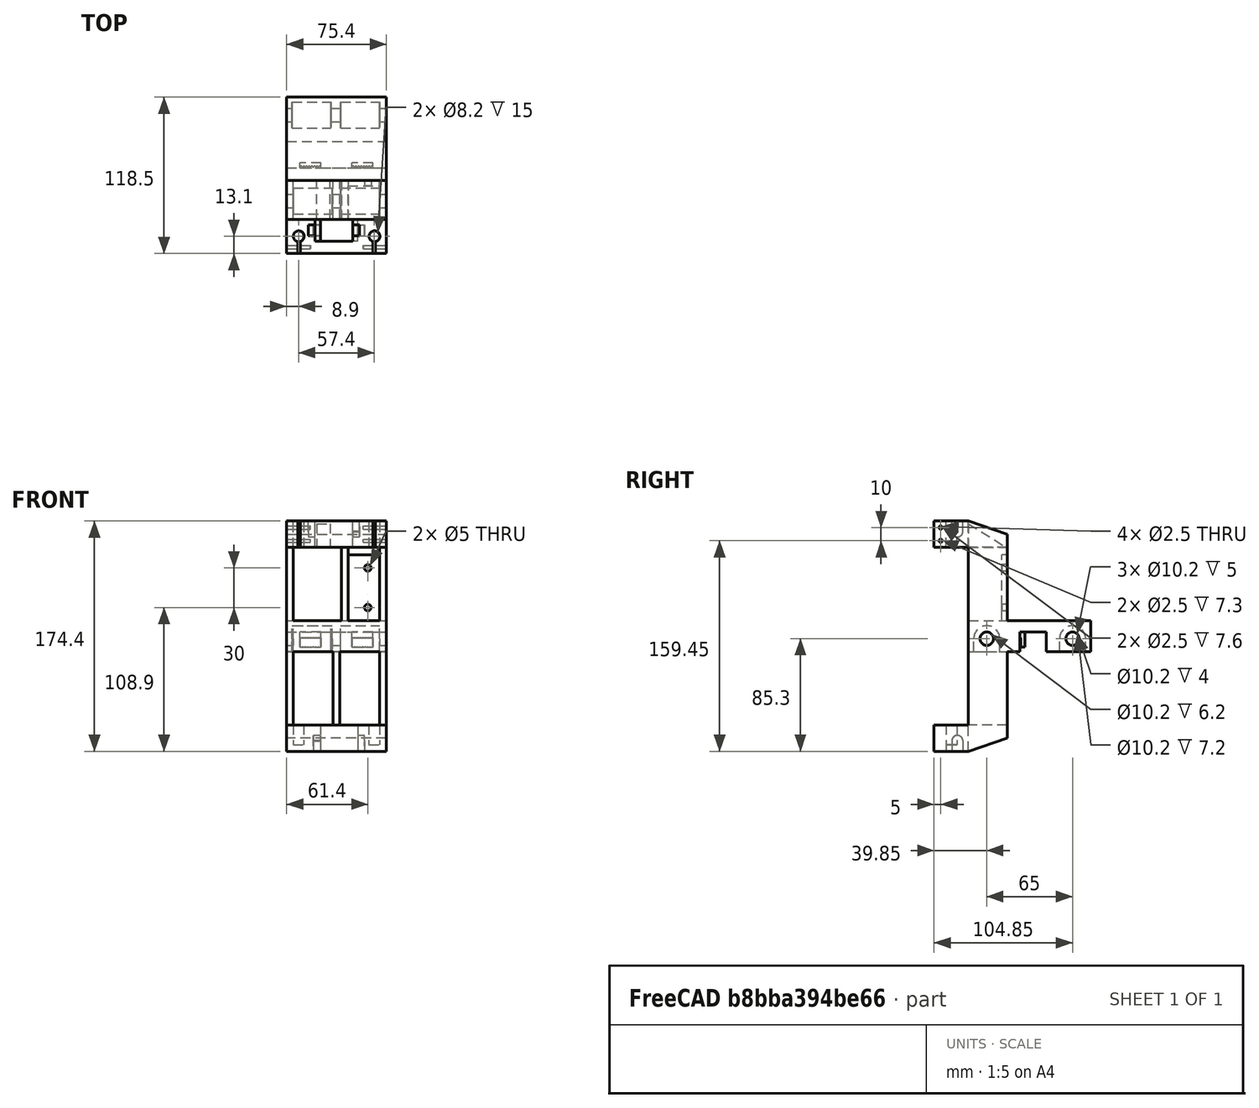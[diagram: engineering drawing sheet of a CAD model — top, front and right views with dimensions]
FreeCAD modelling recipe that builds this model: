
FCSTD DOCUMENT  (FreeCAD 0.18R16110 (Git))
Label: z-support
License: All rights reserved
LicenseURL: http://en.wikipedia.org/wiki/All_rights_reserved
objects: Part::Cut×25, Part::Cylinder×15, Part::Box×13, Part::MultiFuse×11, Part::Wedge×8, Part::Extrusion×8, Spreadsheet::Sheet×2, Sketcher::SketchObject×1, Mesh::Feature×1
note: 81 computed .brp shape members not serialized (recipe doc carries the construction recipe); baked Part::Feature solids carry a one-line shape summary decoded from their .brp

FEATURE [Part::Box] Box007  label="Quader004"
  AttacherType = Attacher::AttachEngine3D
  Height = 10
  Length = 5.2
  Placement = pos=(0,-4.1,0) rot=(0,0,1;0rad)
  Width = 8.2
  expr: Placement.Base.y = -Spreadsheet.z_dbohrung / 2 - Spreadsheet.tolerance / 2
  expr: Height = Spreadsheet.z_hmount / 2
  expr: Width = Spreadsheet.z_dbohrung + Spreadsheet.tolerance
  expr: Length = Spreadsheet.z_lbohrung + Spreadsheet.tolerance
FEATURE [Part::Box] Box012  label="Quader009"
  AttacherType = Attacher::AttachEngine3D
  Height = 9.85
  Length = 29.6
  Placement = pos=(0,-9.85,-9.85) rot=(0,0,1;0rad)
  Width = 19.7
  expr: Placement.Base.z = -Spreadsheet.x_dlinear / 2 - Spreadsheet.tolerance / 2
  expr: Height = Spreadsheet.x_dlinear / 2 + Spreadsheet.tolerance / 2
  expr: Placement.Base.y = -Spreadsheet.x_dlinear / 2 - Spreadsheet.tolerance / 2
  expr: Width = Spreadsheet.x_dlinear + Spreadsheet.tolerance
  expr: Length = Spreadsheet.x_hlinear + Spreadsheet.tolerance
FEATURE [Part::Box] Box008  label="Quader005"
  AttacherType = Attacher::AttachEngine3D
  Height = 10
  Length = 5.2
  Placement = pos=(0,-4.05,0) rot=(0,0,1;0rad)
  Width = 8.2
  expr: Width = Spreadsheet.z_dbohrung + Spreadsheet.tolerance
  expr: Length = Spreadsheet.z_lbohrung + Spreadsheet.tolerance
  expr: Placement.Base.y = -(Spreadsheet.z_dbohrung + Spreadsheet.tolerance / 2) / 2
FEATURE [Part::Cylinder] Cylinder021  label="Zylinder015"
  Angle = 360
  AttacherType = Attacher::AttachEngine3D
  Height = 20
  Placement = pos=(9.1,13.1,0) rot=(0,0,1;0rad)
  Radius = 4.1
  expr: Placement.Base.y = -Spreadsheet.z_bs / 2 + Spreadsheet.z_bmount - Spreadsheet.tolerance
  expr: Placement.Base.x = Spreadsheet.z_swand + Spreadsheet.z_df / 2 + Spreadsheet.tolerance / 2
  expr: Height = Spreadsheet.z_hmount
  expr: Radius = Spreadsheet.z_df / 2 + Spreadsheet.tolerance / 2
FEATURE [Part::Cylinder] Cylinder024  label="Zylinder018"
  Angle = 360
  AttacherType = Attacher::AttachEngine3D
  Height = 5
  Placement = pos=(9,-12.7,-75.45) rot=(0,0,1;0rad)
  Radius = 5
  expr: Placement.Base.z = -(Spreadsheet.z_hub + Spreadsheet.z_hs - Spreadsheet.x_hs) / 2 - 20
  expr: Placement.Base.x = Spreadsheet.z_lmount - Spreadsheet.z_swand - Spreadsheet.z_df / 2 - Spreadsheet.z_sfa
FEATURE [Part::Cylinder] Cylinder020  label="Zylinder014"
  Angle = 360
  AttacherType = Attacher::AttachEngine3D
  Height = 29.6
  Placement = pos=(0,0,0) rot=(0,1,0;1.5708rad)
  Radius = 9.85
  expr: Height = Spreadsheet.x_hlinear + Spreadsheet.tolerance
  expr: Radius = Spreadsheet.x_dlinear / 2 + Spreadsheet.tolerance / 2
FEATURE [Part::Cylinder] Cylinder023  label="Zylinder017"
  Angle = 360
  AttacherType = Attacher::AttachEngine3D
  Height = 5
  Placement = pos=(66.4,-12.7,-75.45) rot=(0,0,1;0rad)
  Radius = 5
  expr: Placement.Base.z = -(Spreadsheet.z_hub + Spreadsheet.z_hs - Spreadsheet.x_hs) / 2 - 20
  expr: Placement.Base.x = Spreadsheet.z_lmount - Spreadsheet.z_swand - Spreadsheet.z_df / 2
FEATURE [Part::Cylinder] Cylinder022  label="Zylinder016"
  Angle = 360
  AttacherType = Attacher::AttachEngine3D
  Height = 20
  Placement = pos=(66.5,13.1,0) rot=(0,0,1;0rad)
  Radius = 4.1
  expr: Placement.Base.y = -Spreadsheet.z_bs / 2 + Spreadsheet.z_bmount - Spreadsheet.tolerance
  expr: Placement.Base.x = Spreadsheet.z_swand + Spreadsheet.z_df / 2 + Spreadsheet.z_sfa + Spreadsheet.tolerance / 2
  expr: Height = Spreadsheet.z_hmount
  expr: Radius = Spreadsheet.z_df / 2 + Spreadsheet.tolerance / 2
FEATURE [Part::MultiFuse] Fusion007
  Placement = pos=(40.8,13.85,9.85) rot=(0,0,1;0rad)
  Shapes = -> [Cylinder020,Box012]
  expr: Placement.Base.x = Spreadsheet.x_ls - Spreadsheet.z_swand - Spreadsheet.x_hlinear - Spreadsheet.tolerance
  expr: Placement.Base.y = Spreadsheet.x_swand + Spreadsheet.x_dlinear / 2 + Spreadsheet.tolerance / 2
  expr: Placement.Base.z = Spreadsheet.x_dlinear / 2 + Spreadsheet.tolerance / 2
FEATURE [Part::MultiFuse] Fusion009
  Placement = pos=(40.8,78.85,9.85) rot=(0,0,1;0rad)
  Shapes = -> [Cylinder020,Box012]
  expr: Placement.Base.x = Spreadsheet.x_ls - Spreadsheet.z_swand - Spreadsheet.x_hlinear - Spreadsheet.tolerance
  expr: Placement.Base.y = Spreadsheet.x_swand + Spreadsheet.x_dlinear / 2 + Spreadsheet.x_sfa + Spreadsheet.tolerance / 2
  expr: Placement.Base.z = Spreadsheet.x_dlinear / 2 + Spreadsheet.tolerance / 2
FEATURE [Part::MultiFuse] Fusion006
  Placement = pos=(5,13.85,9.85) rot=(0,0,1;0rad)
  Shapes = -> [Cylinder020,Box012]
  expr: Placement.Base.x = Spreadsheet.z_swand
  expr: Placement.Base.y = Spreadsheet.x_swand + Spreadsheet.x_dlinear / 2 + Spreadsheet.tolerance / 2
  expr: Placement.Base.z = Spreadsheet.x_dlinear / 2 + Spreadsheet.tolerance / 2
FEATURE [Part::MultiFuse] Fusion008
  Placement = pos=(4,78.85,9.85) rot=(0,0,1;0rad)
  Shapes = -> [Cylinder020,Box012]
  expr: Placement.Base.x = Spreadsheet.x_swand
  expr: Placement.Base.y = Spreadsheet.x_swand + Spreadsheet.x_dlinear / 2 + Spreadsheet.x_sfa + Spreadsheet.tolerance / 2
  expr: Placement.Base.z = Spreadsheet.x_dlinear / 2 + Spreadsheet.tolerance / 2
FEATURE [Part::Cylinder] Cylinder039  label="Zylinder031"
  Angle = 360
  AttacherType = Attacher::AttachEngine3D
  Height = 20
  Placement = pos=(58,-21,84) rot=(0,1,0;1.5708rad)
  Radius = 1.25
FEATURE [Part::Box] Box021  label="Quader013"
  AttacherType = Attacher::AttachEngine3D
  Height = 40
  Length = 2
  Placement = pos=(65.3,-36,67) rot=(0,0,1;0rad)
  Width = 20
FEATURE [Part::Cylinder] Cylinder040  label="Zylinder032"
  Angle = 360
  AttacherType = Attacher::AttachEngine3D
  Height = 20
  Placement = pos=(-2,-21,94) rot=(0,1,0;1.5708rad)
  Radius = 1.25
FEATURE [Part::Box] Box020  label="Quader012"
  AttacherType = Attacher::AttachEngine3D
  Height = 40
  Length = 2
  Placement = pos=(8.4,-36,67) rot=(0,0,1;0rad)
  Width = 20
FEATURE [Part::Cylinder] Cylinder041  label="Zylinder033"
  Angle = 360
  AttacherType = Attacher::AttachEngine3D
  Height = 20
  Placement = pos=(-2,-21,84) rot=(0,1,0;1.5708rad)
  Radius = 1.25
FEATURE [Part::Cylinder] Cylinder042  label="Zylinder034"
  Angle = 360
  AttacherType = Attacher::AttachEngine3D
  Height = 20
  Placement = pos=(58,-21,94) rot=(0,1,0;1.5708rad)
  Radius = 1.25
FEATURE [Part::Box] Box016  label="Zahnriemen002"
  AttacherType = Attacher::AttachEngine3D
  Height = 18
  Length = 10
  Placement = pos=(22.7,-13.4,84.0801) rot=(-1,0,0;0.559338rad)
  Width = 100
  expr: Placement.Rotation.Angle = Spreadsheet.B48
  expr: Placement.Base.x = Spreadsheet.B41 + 1
  expr: Placement.Base.y = Spreadsheet.B26 + -5
  expr: Placement.Base.z = Spreadsheet.B27 - 10 + -5 * tan(Spreadsheet.B48)
FEATURE [Part::Box] Box032  label="Quader023"
  AttacherType = Attacher::AttachEngine3D
  Height = 15
  Length = 75.4
  Placement = pos=(0,38.85,0) rot=(0,0,1;0rad)
  Width = 20
  expr: Placement.Base.y = Spreadsheet.E27 + Spreadsheet.E24 / 2 - Spreadsheet.E45 / 2
  expr: Length = Spreadsheet.x_ls
  expr: Width = 20
FEATURE [Part::Box] Box050  label="Quader029"
  AttacherType = Attacher::AttachEngine3D
  Height = 50
  Length = 34
  Width = 4
  expr: Width = Spreadsheet.x_swand
  expr: Length = Spreadsheet.hnema
FEATURE [Part::Box] Box048  label="Quader027"
  AttacherType = Attacher::AttachEngine3D
  Height = 15
  Length = 16
  Width = 4
FEATURE [Part::Box] Box049  label="Quader028"
  AttacherType = Attacher::AttachEngine3D
  Height = 12
  Length = 16
  Placement = pos=(0,-4.3,-5) rot=(0,0,1;0rad)
  Width = 5
FEATURE [Part::Cylinder] Cylinder062  label="Zylinder051"
  Angle = 360
  AttacherType = Attacher::AttachEngine3D
  Height = 5
  Placement = pos=(20,5,39.95) rot=(1,0,0;1.5708rad)
  Radius = 2.5
  expr: Placement.Base.x = 17 + 3
  expr: Placement.Base.z = 11 + 30 - 1.05
FEATURE [Part::Cylinder] Cylinder063  label="Zylinder052"
  Angle = 360
  AttacherType = Attacher::AttachEngine3D
  Height = 5
  Placement = pos=(20,5,9.95) rot=(1,0,0;1.5708rad)
  Radius = 2.5
  expr: Placement.Base.x = 17 + 3
  expr: Placement.Base.z = 11 - 1.05
FEATURE [Part::Cut] Cut069
  Base = -> Box050
  Tool = -> Cylinder063
FEATURE [Part::Cut] Cut070  label="z_motor_mount"
  Base = -> Cut069
  Placement = pos=(41.4,25.4085,23.5) rot=(0,0,1;0rad)
  Tool = -> Cylinder062
  expr: Placement.Base.z = Spreadsheet.x_hs
  expr: Placement.Base.x = Spreadsheet.x_ls - Spreadsheet.hnema + Spreadsheet.E1
  expr: Placement.Base.y = Spreadsheet.nema_achse_y - 30 + Spreadsheet.H1 - Spreadsheet.x_swand
FEATURE [Part::Box] Box006  label="Quader003"
  AttacherType = Attacher::AttachEngine3D
  Height = 20
  Length = 28.4
  Placement = pos=(21.5,9.2,0) rot=(0,0,1;0rad)
  Width = 17.2
  expr: Placement.Base.y = Spreadsheet.z_swand * 2 - Spreadsheet.tolerance * 4
  expr: Placement.Base.x = Spreadsheet.B41 - Spreadsheet.tolerance
  expr: Height = Spreadsheet.z_hmount
  expr: Width = Spreadsheet.z_driemen + Spreadsheet.tolerance * 6
  expr: Length = Spreadsheet.z_lriemen + Spreadsheet.tolerance * 2
FEATURE [Part::Cylinder] Cylinder015  label="Zylinder011"
  Angle = 360
  AttacherType = Attacher::AttachEngine3D
  Height = 5.2
  Placement = pos=(0,0,0) rot=(0,1,0;1.5708rad)
  Radius = 4.1
  expr: Height = Spreadsheet.z_lbohrung + Spreadsheet.tolerance
  expr: Radius = Spreadsheet.z_dbohrung / 2 + Spreadsheet.tolerance / 2
FEATURE [Part::Cylinder] Cylinder014  label="Zylinder010"
  Angle = 360
  AttacherType = Attacher::AttachEngine3D
  Height = 5.2
  Placement = pos=(0,0,0) rot=(0,1,0;1.5708rad)
  Radius = 4.1
  expr: Height = Spreadsheet.z_lbohrung + Spreadsheet.tolerance
  expr: Radius = Spreadsheet.z_dbohrung / 2 + Spreadsheet.tolerance / 2
FEATURE [Part::Box] Box001  label="x_schlitten"
  AttacherType = Attacher::AttachEngine3D
  Height = 23.5
  Length = 75.4
  Width = 92.5
  expr: Length = Spreadsheet.x_ls
  expr: Height = Spreadsheet.x_hs
  expr: Width = Spreadsheet.x_bs
FEATURE [Part::Cylinder] Cylinder006  label="Zylinder002"
  Angle = 360
  AttacherType = Attacher::AttachEngine3D
  Height = 75.4
  Placement = pos=(0,13.85,9.85) rot=(0,1,0;1.5708rad)
  Radius = 5.1
  expr: Placement.Base.y = Spreadsheet.x_dlinear / 2 + Spreadsheet.x_swand + Spreadsheet.tolerance / 2
  expr: Placement.Base.z = Spreadsheet.x_dlinear / 2 + Spreadsheet.tolerance / 2
  expr: Height = Spreadsheet.x_ls
  expr: Radius = Spreadsheet.x_df / 2 + Spreadsheet.tolerance / 2
FEATURE [Part::Cylinder] Cylinder007  label="Zylinder003"
  Angle = 360
  AttacherType = Attacher::AttachEngine3D
  Height = 75.4
  Placement = pos=(0,78.85,9.85) rot=(0,1,0;1.5708rad)
  Radius = 5.1
  expr: Placement.Base.y = Spreadsheet.x_dlinear / 2 + Spreadsheet.x_swand + Spreadsheet.x_sfa + Spreadsheet.tolerance / 2
  expr: Placement.Base.z = Spreadsheet.x_dlinear / 2 + Spreadsheet.tolerance / 2
  expr: Height = Spreadsheet.x_ls
  expr: Radius = Spreadsheet.x_df / 2 + Spreadsheet.tolerance / 2
FEATURE [Part::Box] Box002  label="z_mount1"
  AttacherType = Attacher::AttachEngine3D
  Height = 20
  Length = 75.4
  Width = 26
  expr: Height = Spreadsheet.z_hmount
  expr: Length = Spreadsheet.z_df + Spreadsheet.z_sfa + 2 * Spreadsheet.z_swand
  expr: Width = Spreadsheet.z_bmount
FEATURE [Part::Cut] Cut011
  Base = -> Box002
  Tool = -> Box006
FEATURE [Part::Cut] Cut013
  Base = -> Cut011
  Tool = -> Cylinder021
FEATURE [Part::Cut] Cut014  label="z_mount_1"
  Base = -> Cut013
  Placement = pos=(0,-0.6,0) rot=(0,0,1;0rad)
  Tool = -> Cylinder022
  expr: Placement.Base.y = Spreadsheet.z_bs - Spreadsheet.z_bmount
FEATURE [Part::MultiFuse] Fusion002
  Placement = pos=(16.5,17,12) rot=(0,0,1;0rad)
  Shapes = -> [Cylinder014,Box007]
  expr: Placement.Base.y = Spreadsheet.z_bs - Spreadsheet.z_driemen / 2 - Spreadsheet.tolerance * 2
  expr: Placement.Base.x = Spreadsheet.B41 - Spreadsheet.z_lbohrung - Spreadsheet.tolerance
  expr: Placement.Base.z = Spreadsheet.z_hmount - Spreadsheet.z_driemen / 2
FEATURE [Part::Cut] Cut015
  Base = -> Cut014
  Tool = -> Fusion002
FEATURE [Part::MultiFuse] Fusion003
  Placement = pos=(49.9,17,12) rot=(0,0,1;0rad)
  Shapes = -> [Cylinder015,Box008]
  expr: Placement.Base.z = Spreadsheet.z_hmount - Spreadsheet.z_driemen / 2
  expr: Placement.Base.y = Spreadsheet.z_bs - Spreadsheet.z_driemen / 2 - Spreadsheet.tolerance * 2
  expr: Placement.Base.x = Spreadsheet.B41 + Spreadsheet.tolerance + Spreadsheet.z_lriemen
FEATURE [Part::Cut] Cut016  label="z_mount1_002"
  Base = -> Cut015
  Placement = pos=(0,-25.4,78.95) rot=(0,0,1;0rad)
  Tool = -> Fusion003
  expr: Placement.Base.z = (Spreadsheet.z_hub + Spreadsheet.z_hs + Spreadsheet.x_hs) / 2
  expr: Placement.Base.y = -Spreadsheet.z_bs
FEATURE [Part::Cut] Cut017  label="z_mount1_003"
  Base = -> Cut015
  Placement = pos=(75.4,-25.4,-55.45) rot=(0,1,0;3.14159rad)
  Tool = -> Fusion003
  expr: Placement.Base.x = Spreadsheet.z_lmount
  expr: Placement.Base.y = -Spreadsheet.z_bs
  expr: Placement.Base.z = -(Spreadsheet.z_hub + Spreadsheet.z_hs - Spreadsheet.x_hs) / 2
FEATURE [Part::MultiFuse] Fusion010
  Shapes = -> [Cut017,Cylinder023]
FEATURE [Part::MultiFuse] Fusion011  label="z_mount2"
  Shapes = -> [Fusion010,Cylinder024]
  expr: Placement.Base.x = +Spreadsheet.E1
  expr: Placement.Base.y = +Spreadsheet.H1
FEATURE [Part::Cut] Cut031
  Base = -> Cut016
  Tool = -> Box020
FEATURE [Part::Cut] Cut032
  Base = -> Cut031
  Tool = -> Box021
FEATURE [Part::Cut] Cut033
  Base = -> Cut032
  Tool = -> Cylinder039
FEATURE [Part::Cut] Cut034
  Base = -> Cut033
  Tool = -> Cylinder040
FEATURE [Part::Cut] Cut035
  Base = -> Cut034
  Tool = -> Cylinder041
FEATURE [Part::Cut] Cut036  label="z_mount_top"
  Base = -> Cut035
  Tool = -> Cylinder042
  expr: Placement.Base.x = +Spreadsheet.E1
  expr: Placement.Base.y = +Spreadsheet.H1
FEATURE [Spreadsheet::Sheet] Spreadsheet
  cells = A1=Toleranz; B1(tolerance)=0.2; D1=x_pos; E1=0; G1=y_pos; H1=0; A2=z_pos; B2=-10; E2=min 0 / max 297; G2=min y_pos; H2=94; I2=max 560; A3=Z-Support; D3=X-Support; G3=y-Support; J3=structure; A4=Führung d; B4(z_df)=8; D4=Führung d; E4(x_df)=10; G4=Führung d; H4(y_df)=10; J4=profil B; K4=20; A5=Führung l; B5(z_fl)==Spreadsheet.z_hub + Spreadsheet.z_hmount * 2 + Spreadsheet.z_hs - 5; D5=Führung l; E5(x_lf)=420; F5=400; G5=Führung l; H5(y_fl)=700; I5=500; J5=distanz Führung; K5=3; A6=Abstand Führung z_sfa; B6(z_sfa)==(z_dlinear + 2 * z_swand + 2 * z_sriemenspiel + z_lriemen) * 1 + (2 * x_hlinear + +z_swand - z_df + 4 * tolerance) * 0; D6=Abstand Führung x_sfa; E6(x_sfa)=65; G6=Abstand Fü y_sfa; H6(y_sfa)==x_lf - x_dlinear - 2 * y_swand; J6=höhe; K6=300; J7=add to Top; K7=18; A8=Schlittenwand swand; B8(z_swand)=5; D8=Schlitten swand; E8(x_swand)=4; G8=y_swand; H8(y_swand)=5; A9=Schlittenlänge z_ls; B9(z_ls)==z_sfa + z_dlinear; D9=Schlittenlänge; E9(x_ls)==z_lmount; A10=Schlittenbreite z_bs; B10(z_bs)==2 * z_swand + z_dlinear; D10=Schlitten breite; E10(x_bs)==Spreadsheet.x_swand * 2 + Spreadsheet.x_dlinear + Spreadsheet.x_sfa; G10=d Antrieb; H10=5; A11=Schlittenhöhe z_hs; B11(z_hs)==z_hlinear + 2 * z_swand; D11=schlittenhöhe x_hs; E11(x_hs)==x_dlinear + x_swand; A12=Hub; B12(z_hub)=100; A14=Linearlager; A15=durchmesser z_dlinear; B15(z_dlinear)=15.4; D15=durchmesser x_dlinear; E15(x_dlinear)=19.5; A16=höhe z_hlinear; B16(z_hlinear)=24.4; D16=höhe x_hlinear; E16(x_hlinear)=29.4; A18=Riemenscheibe bohrung; B18=5; A19=durchmesser z_driemen; B19(z_driemen)=16; D19=dopper pulley; E19=27.5; F19=15.8; A20=länge z_lriemen; B20(z_lriemen)=28; D20=pulley; E20=15.25; F20=15.8; G20=20 Zähne: 2* 180 °; H20=2mm*20 Zähne; I20==40mm; A21=spiel riemenscheibe z_sriemenspiel; B21(z_sriemenspiel)=2; A22=Bohreung z_dbohrung; B22(z_dbohrung)=8; C22=durchmesser Laufbuchse; D22=x_mount; A23=Bohrunlänge z_lbohrung; B23(z_lbohrung)=5; D23=Breite x_mount; E23==y_swand + x_dlinear; A24=riemenbreite z_briemen; B24(z_briemen)=6; D24=Länge x_mount; E24==x_sfa + x_df + y_swand * 2; A25=pitch z_rriemenpitch; B25(z_rriemepitch)=7; D25=Höhe x_mount; E25==y_swand * 2 + x_df + +y_swand + x_dlinear + y_swand; A26=achsen pos y; B26==-Spreadsheet.z_driemen / 2 - Spreadsheet.tolerance * 2; D26= xpos; E26==-Spreadsheet.E23; A27=achsen pos z; B27==(Spreadsheet.z_hub + Spreadsheet.z_hs + Spreadsheet.x_hs) / 2 + z_hmount - z_dbohrung / 2 - Spreadsheet.z_dbohrung / 2; D27=ypos; E27==Spreadsheet.x_swand + Spreadsheet.x_dlinear / 2 + Spreadsheet.tolerance / 2 - Spreadsheet.x_df / 2 - Spreadsheet.y_swand; D28= zpos; E28==-y_swand; A29=Mount; A30=Höhe mount; B30(z_hmount)=20; A31=Länge mount; B31(z_lmount)==z_swand * 2 + z_df + z_sfa; A32=Breite mount; B32(z_bmount)==(Spreadsheet.z_swand + Spreadsheet.z_driemen + Spreadsheet.tolerance * 2) * 0 + 26; A34=Nema; D34=Nema x; A35=Länge; B35(lnema)=42; D35(nema_x_b)=42; A36=Breite; B36(bnema)=42; D36=42; A37=Höhe; B37(hnema)=34; D37(nema_x_h)=48; A38=Achslänge; B38(lanema)=20; D38(nema_x_al)=22; A39=achsen pos y; B39(nema_achse_y)==sqrt(B43 ^ 2 - (B27 - B40) ^ 2) + B26; E39(nemax_achsey)==Spreadsheet.x_swand + Spreadsheet.x_df / 2 + Spreadsheet.x_dlinear / 2 + Spreadsheet.nema_x_h + 2; A40=achsen pos z; B40(nema_achse_z)==x_hs + lnema / 2 + 4; E40(nema_x_achsez)==-Spreadsheet.x_hs / 2; A41=achsen pos x; B41(nema_achse_x)==(z_lmount - z_lriemen) / 2 - z_sriemenspiel; E41(nema_x_achsex)==Spreadsheet.x_lf - Spreadsheet.nema_x_b / 2 - Spreadsheet.y_df; A42=länge zahnriemen; B42=200; C42=gerechnet; A43=abstand achsen; B43==(B42 - 40) / 2; C43==sqrt((Spreadsheet.B27 - Spreadsheet.nema_achse_z) ^ 2 + (-Spreadsheet.B26 + Spreadsheet.nema_achse_y) ^ 2) * 2 + 2 * pi * 7; D43=Zahnriemen x; D44=Breite; E44=6; A45=doppel pulley; D45=Höhe; E45==(Spreadsheet.F20 + Spreadsheet.tolerance * 2) * 0 + 15; A46= achse1  x pos; B46==z_lmount / 2 - (6.5 + 8.9) / 2; D46=Länge; E46==y_sfa + x_dlinear + y_swand * 2 + 2 + nema_x_b / 2; A47= achse2 xpos; B47==z_lmount / 2 + (6.5 + 8.9) / 2; B48==-atan((Spreadsheet.B27 - Spreadsheet.nema_achse_z) / (-Spreadsheet.B26 + Spreadsheet.nema_achse_y))
FEATURE [Spreadsheet::Sheet] Spreadsheet001
  cells = A1=abstand zähne; B1=2; A2=dicke; B2=1.38; A3=zahntiefe; B3=0.75; A4=r1; B4=0.555; A5=r2; B5=1; A6=r3; B6=0.15; A7=pitch; B7=0.254; A8=tolerance; B8=0.1
FEATURE [Part::Wedge] Wedge006  label="wange_006"
  AttacherType = Attacher::AttachEngine3D
  Placement = pos=(75.4,0,0) rot=(0,1,0;3.14159rad)
  X2max = 5
  X2min = 0
  Xmax = 5
  Xmin = 0
  Ymax = 29.4085
  Ymin = 0
  Z2max = 59.1398
  Z2min = 0
  Zmax = 75.45
  Zmin = 0
  expr: Placement.Base.y = +Spreadsheet.H1
  expr: Placement.Base.x = Spreadsheet.x_ls + Spreadsheet.E1
  expr: X2max = Spreadsheet.z_swand
  expr: Z2max = (Spreadsheet.z_hub + Spreadsheet.z_hs - Spreadsheet.x_hs) / 2 + Spreadsheet.z_hmount - Spreadsheet.x_bs * tan(10)
  expr: Xmax = Spreadsheet.z_swand
  expr: Zmax = (Spreadsheet.z_hub + Spreadsheet.z_hs - Spreadsheet.x_hs) / 2 + Spreadsheet.z_hmount
  expr: Ymax = Spreadsheet.nema_achse_y - 30
FEATURE [Part::Wedge] Wedge005  label="wange_005"
  AttacherType = Attacher::AttachEngine3D
  Placement = pos=(0,0,78.95) rot=(0,0,1;0rad)
  X2max = 75.4
  X2min = 0
  Xmax = 75.4
  Xmin = 0
  Ymax = 29.4085
  Ymin = 0
  Z2max = 10
  Z2min = 0
  Zmax = 20
  Zmin = 0
  expr: Z2max = 10
  expr: X2max = Spreadsheet.z_lmount
  expr: Ymax = Spreadsheet.nema_achse_y - 30
  expr: Zmax = Spreadsheet.z_hmount
  expr: Placement.Base.z = (Spreadsheet.z_hub + Spreadsheet.z_hs + Spreadsheet.x_hs) / 2
  expr: Xmax = Spreadsheet.z_lmount
FEATURE [Part::Cut] Cut025  label="wange_top"
  Base = -> Wedge005
  Tool = -> Box016
  expr: Placement.Base.x = +Spreadsheet.E1
  expr: Placement.Base.y = +Spreadsheet.H1
FEATURE [Part::Wedge] Wedge007  label="wange_007"
  AttacherType = Attacher::AttachEngine3D
  Placement = pos=(5,0,0) rot=(0,1,0;3.14159rad)
  X2max = 5
  X2min = 0
  Xmax = 5
  Xmin = 0
  Ymax = 29.4085
  Ymin = 0
  Z2max = 59.1398
  Z2min = 0
  Zmax = 75.45
  Zmin = 0
  expr: Placement.Base.y = +Spreadsheet.H1
  expr: Placement.Base.x = Spreadsheet.z_swand + Spreadsheet.E1
  expr: X2max = Spreadsheet.z_swand
  expr: Z2max = (Spreadsheet.z_hub + Spreadsheet.z_hs - Spreadsheet.x_hs) / 2 + Spreadsheet.z_hmount - Spreadsheet.x_bs * tan(10)
  expr: Xmax = Spreadsheet.z_swand
  expr: Zmax = (Spreadsheet.z_hub + Spreadsheet.z_hs - Spreadsheet.x_hs) / 2 + Spreadsheet.z_hmount
  expr: Ymax = Spreadsheet.nema_achse_y - 30
FEATURE [Part::Wedge] Wedge008  label="wange_008"
  AttacherType = Attacher::AttachEngine3D
  Placement = pos=(75.4,0,-55.45) rot=(0,1,0;3.14159rad)
  X2max = 75.4
  X2min = 0
  Xmax = 75.4
  Xmin = 0
  Ymax = 29.4085
  Ymin = 0
  Z2max = 10
  Z2min = 0
  Zmax = 20
  Zmin = 0
  expr: Placement.Base.y = +Spreadsheet.H1
  expr: Placement.Base.x = Spreadsheet.z_lmount + Spreadsheet.E1
  expr: Z2max = 10
  expr: Placement.Base.z = -((Spreadsheet.z_hub + Spreadsheet.z_hs - Spreadsheet.x_hs) / 2)
  expr: X2max = Spreadsheet.z_lmount
  expr: Ymax = Spreadsheet.nema_achse_y - 30
  expr: Zmax = Spreadsheet.z_hmount
  expr: Xmax = Spreadsheet.z_lmount
FEATURE [Part::Wedge] Wedge002  label="wange_2"
  AttacherType = Attacher::AttachEngine3D
  Placement = pos=(70.4,0,23.5) rot=(0,1,0;0rad)
  X2max = 5
  X2min = 0
  Xmax = 5
  Xmin = 0
  Ymax = 29.4085
  Ymin = 0
  Z2max = 59.1398
  Z2min = 0
  Zmax = 75.45
  Zmin = 0
  expr: Placement.Base.y = +Spreadsheet.H1
  expr: Placement.Base.x = Spreadsheet.x_ls - Spreadsheet.z_swand + Spreadsheet.E1
  expr: Ymax = Spreadsheet.nema_achse_y - 30
  expr: Zmax = (Spreadsheet.z_hub + Spreadsheet.z_hs - Spreadsheet.x_hs) / 2 + Spreadsheet.z_hmount
  expr: X2max = Spreadsheet.z_swand
  expr: Placement.Base.z = Spreadsheet.x_hs
  expr: Z2max = (Spreadsheet.z_hub + Spreadsheet.z_hs - Spreadsheet.x_hs) / 2 + Spreadsheet.z_hmount - Spreadsheet.x_bs * tan(10)
  expr: Xmax = Spreadsheet.z_swand
FEATURE [Part::Wedge] Wedge001  label="wange_1"
  AttacherType = Attacher::AttachEngine3D
  Placement = pos=(0,0,23.5) rot=(0,1,0;0rad)
  X2max = 5
  X2min = 0
  Xmax = 5
  Xmin = 0
  Ymax = 29.4085
  Ymin = 0
  Z2max = 59.1398
  Z2min = 0
  Zmax = 75.45
  Zmin = 0
  expr: Placement.Base.y = +Spreadsheet.H1
  expr: Placement.Base.x = +Spreadsheet.E1
  expr: X2max = Spreadsheet.z_swand
  expr: Z2max = (Spreadsheet.z_hub + Spreadsheet.z_hs - Spreadsheet.x_hs) / 2 + Spreadsheet.z_hmount - Spreadsheet.x_bs * tan(10)
  expr: Placement.Base.z = Spreadsheet.x_hs
  expr: Xmax = Spreadsheet.z_swand
  expr: Zmax = (Spreadsheet.z_hub + Spreadsheet.z_hs - Spreadsheet.x_hs) / 2 + Spreadsheet.z_hmount
  expr: Ymax = Spreadsheet.nema_achse_y - 30
FEATURE [Part::Wedge] Wedge010  label="wange_010"
  AttacherType = Attacher::AttachEngine3D
  Placement = pos=(40.2,0,0) rot=(0,1,0;3.14159rad)
  X2max = 5
  X2min = 0
  Xmax = 5
  Xmin = 0
  Ymax = 29.4085
  Ymin = 0
  Z2max = 59.1398
  Z2min = 0
  Zmax = 75.45
  Zmin = 0
  expr: Placement.Base.y = +Spreadsheet.H1
  expr: Placement.Base.x = Spreadsheet.z_swand / 2 + Spreadsheet.x_ls / 2 + Spreadsheet.E1
  expr: X2max = Spreadsheet.z_swand
  expr: Z2max = (Spreadsheet.z_hub + Spreadsheet.z_hs - Spreadsheet.x_hs) / 2 + Spreadsheet.z_hmount - Spreadsheet.x_bs * tan(10)
  expr: Xmax = Spreadsheet.z_swand
  expr: Zmax = (Spreadsheet.z_hub + Spreadsheet.z_hs - Spreadsheet.x_hs) / 2 + Spreadsheet.z_hmount
  expr: Ymax = Spreadsheet.nema_achse_y - 30
FEATURE [Part::Wedge] Wedge009  label="wange_009"
  AttacherType = Attacher::AttachEngine3D
  Placement = pos=(41.4,0,23.5) rot=(0,0,1;0rad)
  X2max = 5
  X2min = 0
  Xmax = 5
  Xmin = 0
  Ymax = 29.4085
  Ymin = 0
  Z2max = 59.1398
  Z2min = 0
  Zmax = 75.45
  Zmin = 0
  expr: Placement.Base.y = +Spreadsheet.H1
  expr: Placement.Base.x = Spreadsheet.x_ls - Spreadsheet.hnema + Spreadsheet.E1
  expr: X2max = Spreadsheet.z_swand
  expr: Z2max = (Spreadsheet.z_hub + Spreadsheet.z_hs - Spreadsheet.x_hs) / 2 + Spreadsheet.z_hmount - Spreadsheet.x_bs * tan(10)
  expr: Placement.Base.z = Spreadsheet.x_hs
  expr: Xmax = Spreadsheet.z_swand
  expr: Zmax = (Spreadsheet.z_hub + Spreadsheet.z_hs - Spreadsheet.x_hs) / 2 + Spreadsheet.z_hmount
  expr: Ymax = Spreadsheet.nema_achse_y - 30
FEATURE [Sketcher::SketchObject] Sketch
  MapMode = 2
  Placement = pos=(0,0,0) rot=(0,1,0;3.14159rad)
  expr: Constraints[11] = Spreadsheet001.B5
  expr: Constraints[30] = Spreadsheet001.B1 / 2
  expr: Constraints[25] = Spreadsheet001.B2 - Spreadsheet001.B3
  expr: Constraints[16] = Spreadsheet001.B2 - Spreadsheet001.B3
  expr: Constraints[18] = Spreadsheet001.B6
  expr: Constraints[36] = Spreadsheet001.B6
  expr: Constraints[33] = Spreadsheet001.B2 - Spreadsheet001.B3
  expr: Constraints[17] = Spreadsheet001.B1 / 2
  expr: Constraints[9] = Spreadsheet001.B2 - Spreadsheet001.B3
  expr: Constraints[2] = Spreadsheet001.B2 - Spreadsheet001.B4
  sketch-geometry (16):
    g0: LineSegment [constr] StartX=0 StartY=0 StartZ=0 EndX=0 EndY=-0.825 EndZ=0
    g1: ArcOfCircle CenterX=0 CenterY=-0.825 CenterZ=0 NormalX=0 NormalY=0 NormalZ=1 AngleXU=0 Radius=0.555 StartAngle=3.59519 EndAngle=5.82959
    g2: LineSegment [constr] StartX=0 StartY=0 StartZ=0 EndX=0.4 EndY=0 EndZ=0
    g3: LineSegment [constr] StartX=0.4 StartY=0 StartZ=0 EndX=0.4 EndY=-0.63 EndZ=0
    g4: ArcOfCircle CenterX=0.4 CenterY=-0.63 CenterZ=0 NormalX=0 NormalY=0 NormalZ=1 AngleXU=0 Radius=1 StartAngle=3.2724 EndAngle=3.59519
    g5: LineSegment StartX=0 StartY=0 StartZ=0 EndX=-1 EndY=0 EndZ=0
    g6: LineSegment StartX=-1 StartY=0 StartZ=0 EndX=-1 EndY=-0.63 EndZ=0
    g7: ArcOfCircle CenterX=-0.740175 CenterY=-0.78 CenterZ=0 NormalX=0 NormalY=0 NormalZ=1 AngleXU=0 Radius=0.15 StartAngle=0.130807 EndAngle=1.5708
    g8: LineSegment StartX=-1 StartY=-0.63 StartZ=0 EndX=-0.740175 EndY=-0.63 EndZ=0
    g9: LineSegment [constr] StartX=0 StartY=0 StartZ=0 EndX=-0.4 EndY=0 EndZ=0
    g10: LineSegment [constr] StartX=-0.4 StartY=0 StartZ=0 EndX=-0.4 EndY=-0.63 EndZ=0
    g11: ArcOfCircle CenterX=-0.4 CenterY=-0.63 CenterZ=0 NormalX=0 NormalY=0 NormalZ=1 AngleXU=0 Radius=1 StartAngle=5.82959 EndAngle=6.15238
    g12: LineSegment StartX=0 StartY=0 StartZ=0 EndX=1 EndY=0 EndZ=0
    g13: LineSegment StartX=1 StartY=0 StartZ=0 EndX=1 EndY=-0.63 EndZ=0
    g14: LineSegment StartX=1 StartY=-0.63 StartZ=0 EndX=0.740175 EndY=-0.63 EndZ=0
    g15: ArcOfCircle CenterX=0.740175 CenterY=-0.78 CenterZ=0 NormalX=0 NormalY=0 NormalZ=1 AngleXU=0 Radius=0.15 StartAngle=1.5708 EndAngle=3.01079
  constraints (43):
    c: Coincident(g0,g-1)
    c: Vertical(g0)
    c: DistanceY(g0,g0) = 0.825
    c: Coincident(g1,g0)
    c: Coincident(g2,g-1)
    c: Horizontal(g2)
    c: DistanceX(g2,g2) = 0.4
    c: Coincident(g3,g2)
    c: Vertical(g3)
    c: DistanceY(g3,g3) = 0.63
    c: Coincident(g4,g3)
    c: Radius(g4) = 1
    c: Coincident(g5,g-1)
    c: Horizontal(g5)
    c: Coincident(g6,g5)
    c: Vertical(g6)
    c: DistanceY(g6,g6) = 0.63
    c: DistanceX(g5,g5) = 1
    c: Radius(g7) = 0.15
    c: Coincident(g8,g6)
    c: Horizontal(g8)
    c: Coincident(g9,g-1)
    c: Distance(g9) = 0.4
    c: Coincident(g10,g9)
    c: Vertical(g10)
    c: DistanceY(g10,g10) = 0.63
    c: Horizontal(g9)
    c: Coincident(g11,g10)
    c: Coincident(g12,g-1)
    c: Horizontal(g12)
    c: DistanceX(g12,g12) = 1
    c: Coincident(g13,g12)
    c: Vertical(g13)
    c: DistanceY(g13,g13) = 0.63
    c: Coincident(g14,g13)
    c: Horizontal(g14)
    c: Radius(g15) = 0.15
    c: Tangent(g15,g14) = -1.5708
    c: Tangent(g7,g8) = 1.5708
    c: Tangent(g7,g4) = 1.5708
    c: Tangent(g15,g11) = 1.5708
    c: Tangent(g4,g1) = -1.5708
    c: Tangent(g11,g1) = -1.5708
FEATURE [Part::Extrusion] Extrude001
  Base = -> Sketch
  Dir = (0,0,-1)
  DirMode = 2
  FaceMakerClass = Part::FaceMakerBullseye
  LengthFwd = 7
  LengthRev = 0
  Placement = pos=(2,0,0) rot=(0,0,1;0rad)
  Solid = true
  Symmetric = false
FEATURE [Part::Extrusion] Extrude003
  Base = -> Sketch
  Dir = (0,0,-1)
  DirMode = 2
  FaceMakerClass = Part::FaceMakerBullseye
  LengthFwd = 7
  LengthRev = 0
  Placement = pos=(6,0,0) rot=(0,0,1;0rad)
  Solid = true
  Symmetric = false
FEATURE [Part::Extrusion] Extrude004
  Base = -> Sketch
  Dir = (0,0,-1)
  DirMode = 2
  FaceMakerClass = Part::FaceMakerBullseye
  LengthFwd = 7
  LengthRev = 0
  Placement = pos=(10,0,0) rot=(0,0,1;0rad)
  Solid = true
  Symmetric = false
FEATURE [Part::Extrusion] Extrude
  Base = -> Sketch
  Dir = (0,0,-1)
  DirMode = 2
  FaceMakerClass = Part::FaceMakerBullseye
  LengthFwd = 7
  LengthRev = 0
  Solid = true
  Symmetric = false
FEATURE [Part::Extrusion] Extrude007
  Base = -> Sketch
  Dir = (0,0,-1)
  DirMode = 2
  FaceMakerClass = Part::FaceMakerBullseye
  LengthFwd = 7
  LengthRev = 0
  Placement = pos=(12,0,0) rot=(0,0,1;0rad)
  Solid = true
  Symmetric = false
FEATURE [Part::Extrusion] Extrude002
  Base = -> Sketch
  Dir = (0,0,-1)
  DirMode = 2
  FaceMakerClass = Part::FaceMakerBullseye
  LengthFwd = 7
  LengthRev = 0
  Placement = pos=(4,0,0) rot=(0,0,1;0rad)
  Solid = true
  Symmetric = false
FEATURE [Part::Extrusion] Extrude005
  Base = -> Sketch
  Dir = (0,0,-1)
  DirMode = 2
  FaceMakerClass = Part::FaceMakerBullseye
  LengthFwd = 7
  LengthRev = 0
  Placement = pos=(8,0,0) rot=(0,0,1;0rad)
  Solid = true
  Symmetric = false
FEATURE [Part::Extrusion] Extrude006
  Base = -> Sketch
  Dir = (0,0,-1)
  DirMode = 2
  FaceMakerClass = Part::FaceMakerBullseye
  LengthFwd = 7
  LengthRev = 0
  Placement = pos=(14,0,0) rot=(0,0,1;0rad)
  Solid = true
  Symmetric = false
FEATURE [Part::MultiFuse] Fusion030  label="Form Zahnriemen"
  Placement = pos=(15,0.1,7) rot=(0,0,1;3.14159rad)
  Shapes = -> [Extrude005,Extrude002,Extrude003,Extrude,Extrude001,Extrude004,Extrude007,Extrude006]
FEATURE [Part::Cut] Cut059
  Base = -> Box048
  Tool = -> Fusion030
FEATURE [Part::Cut] Cut064  label="Zahnriemen Befestigung004"
  Base = -> Cut059
  Placement = pos=(10,38.85,3.5) rot=(0.008727,0.999962,0;0rad)
  Tool = -> Box049
  expr: Placement.Base.y = Spreadsheet.E27 + Spreadsheet.E24 / 2 + Spreadsheet.E45 / 2 - Spreadsheet.E45
  expr: Placement.Base.x = 10
FEATURE [Part::Cut] Cut065  label="Zahnriemen Befestigung005"
  Base = -> Cut059
  Placement = pos=(49.4,38.85,3.5) rot=(0,0,1;0rad)
  Tool = -> Box049
  expr: Placement.Base.y = Spreadsheet.E27 + Spreadsheet.E24 / 2 + Spreadsheet.E45 / 2 - Spreadsheet.E45
  expr: Placement.Base.x = +Spreadsheet.x_ls - 16 - 10
FEATURE [Part::Cut] Cut002
  Base = -> Box001
  Tool = -> Cylinder006
FEATURE [Part::Cut] Cut003  label="x_schlitten001"
  Base = -> Cut002
  Tool = -> Cylinder007
FEATURE [Part::Cut] Cut019
  Base = -> Cut003
  Tool = -> Fusion006
FEATURE [Part::Cut] Cut020
  Base = -> Cut019
  Tool = -> Fusion007
FEATURE [Part::Cut] Cut021
  Base = -> Cut020
  Tool = -> Fusion008
FEATURE [Part::Cut] Cut022  label="x_schlitten002"
  Base = -> Cut021
  Tool = -> Fusion009
FEATURE [Part::Cut] Cut057  label="x_schlitten003"
  Base = -> Cut022
  Tool = -> Box032
FEATURE [Part::MultiFuse] Fusion033  label="x_schliitten"
  Shapes = -> [Cut057,Cut064,Cut065]
  expr: Placement.Base.y = +Spreadsheet.H1
  expr: Placement.Base.x = +Spreadsheet.E1
FEATURE [Part::MultiFuse] Fusion  label="z-support"
  Shapes = -> [Fusion011,Wedge006,Wedge009,Wedge007,Wedge008,Wedge002,Wedge001,Wedge010,Cut070,Cut036,Fusion033,Cut025]
FEATURE [Mesh::Feature] Mesh  label="z-support (Meshed)"
